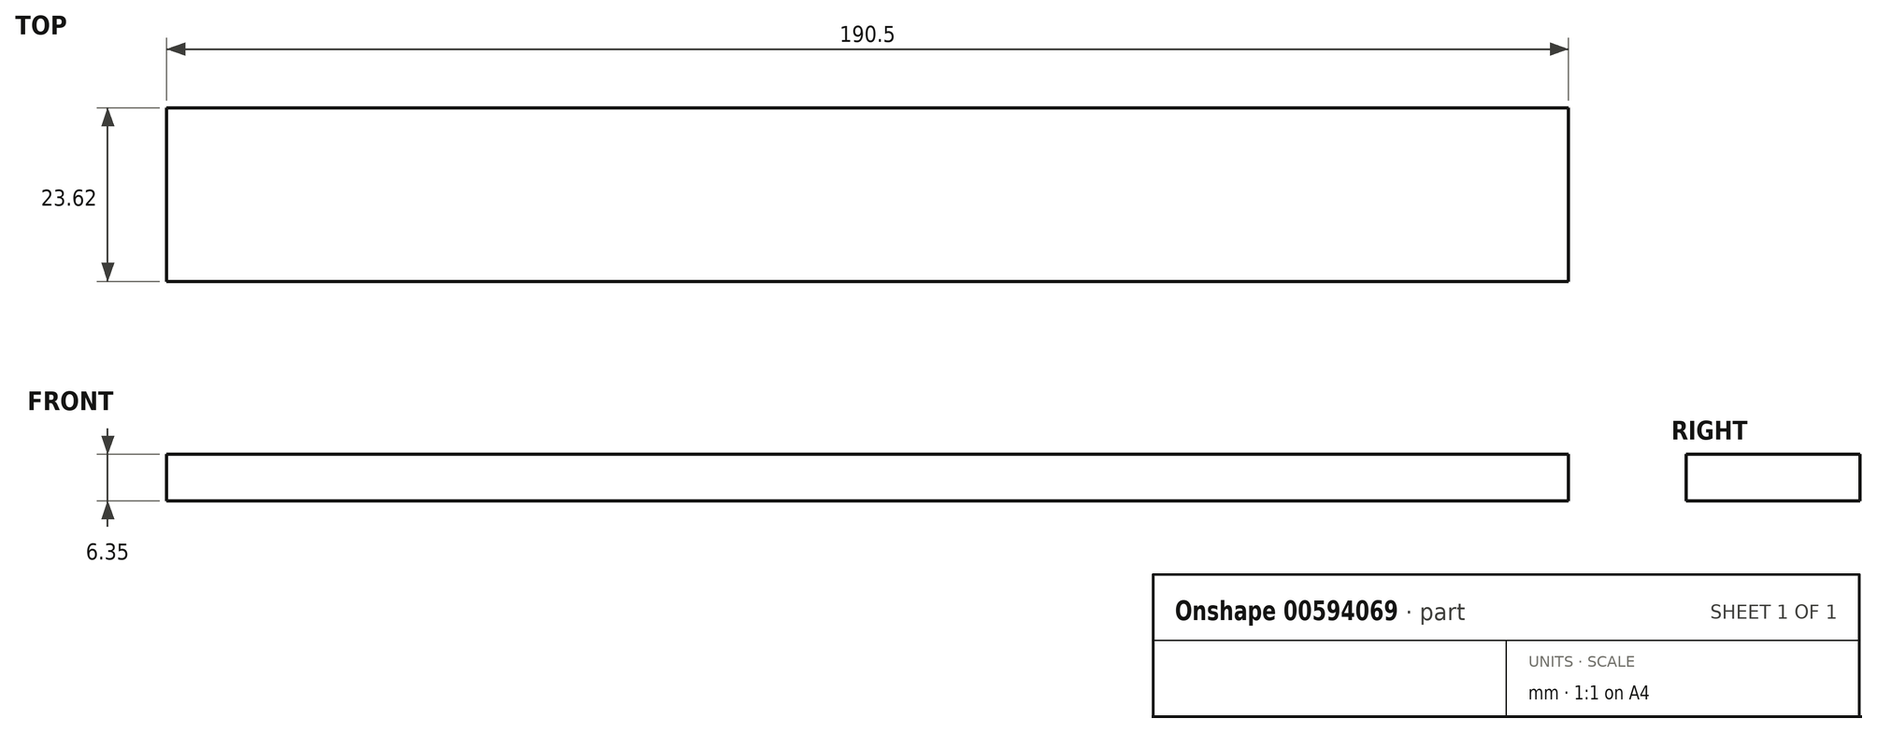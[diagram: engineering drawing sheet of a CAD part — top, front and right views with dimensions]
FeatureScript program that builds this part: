
annotation { "Feature Type Name" : "Feature", "Feature Type Description" : "" }
export const myFeature = defineFeature(function(context is Context, id is Id, definition is map)
    precondition{}
    {
        {
            var Q0;
            Q0=qCreatedBy(makeId("Top.planeOp"),FACE);
            var sketch = newSketch(context, id + "F0", { "sketchPlane" : qUnion([Q0])});
            skLineSegment(sketch, "E0.bottom", {"start": v(0, 0) * mm, "end": v(190.5, 0) * mm});
            skLineSegment(sketch, "E0.top", {"start": v(0, -23.62) * mm, "end": v(190.5, -23.62) * mm});
            skLineSegment(sketch, "E0.left", {"start": v(0, 0) * mm, "end": v(0, -23.62) * mm});
            skLineSegment(sketch, "E0.right", {"start": v(190.5, 0) * mm, "end": v(190.5, -23.62) * mm});
            skSolve(sketch);
        }
        {
            var Q0;
            Q0=makeQuery(id+"F0.imprint","IMPRINT",FACE,{"disambiguationData":[TD([[makeQuery(id+"F0.imprint","IMPRINT",EDGE,{"derivedFrom":sQuery(id+"F0.wireOp",EDGE,"E0.bottom")}),-1.0]])]});
            extrude(context, id + "F1", {"entities" : qUnion([Q0]), "depth" : 6.35 * mm, "offsetDistance" : 25.4 * mm});
        }
    });
